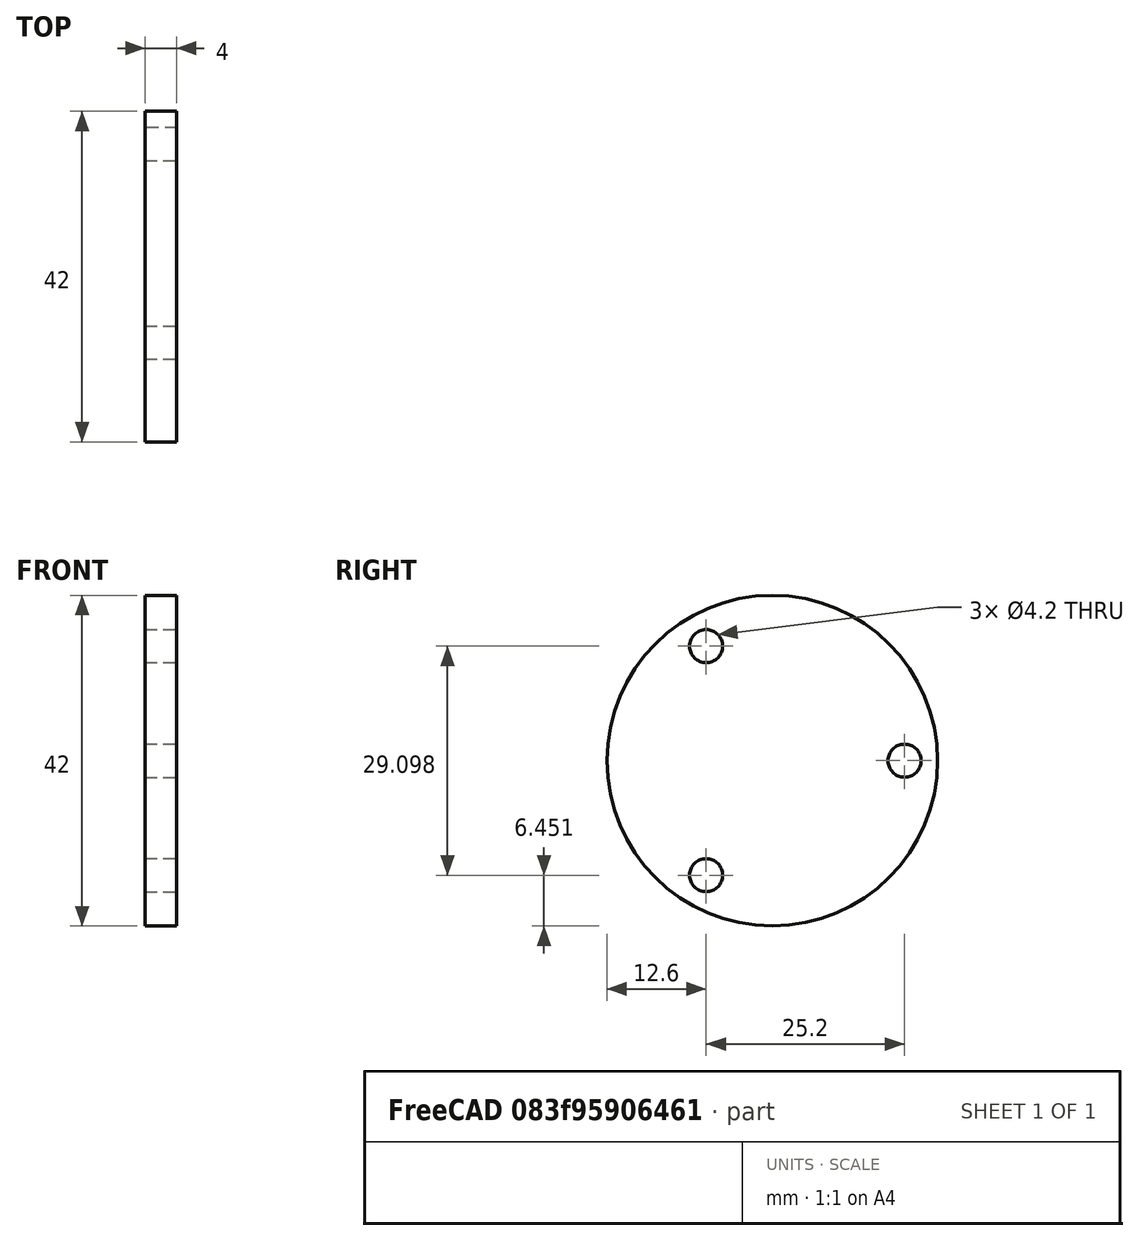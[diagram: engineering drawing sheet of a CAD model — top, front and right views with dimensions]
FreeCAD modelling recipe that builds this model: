
FCSTD DOCUMENT  (FreeCAD 0.19R21329 (Git))
Label: progetto
License: All rights reserved
LicenseURL: http://en.wikipedia.org/wiki/All_rights_reserved
objects: PartDesign::Body×2, Sketcher::SketchObject×2, Mesh::Feature×2, Part::Feature×1, PartDesign::Pad×1, PartDesign::Pocket×1, PartDesign::PolarPattern×1
note: 10 computed .brp shape members not serialized (recipe doc carries the construction recipe); baked Part::Feature solids carry a one-line shape summary decoded from their .brp

FEATURE [Part::Feature] Solid
  Placement = pos=(-4,0,0) rot=(0.57735,0.57735,0.57735;0rad)
  shape: bbox 21 x 16.5 x 15 mm, 4090 faces (baked)
FEATURE [PartDesign::Body] Body
  Group = -> [Solid]
  Origin = -> Origin
  Placement = pos=(0,-5,-7) rot=(0,0,1;0rad)
FEATURE [Sketcher::SketchObject] Sketch
  MapMode = 5
  Placement = pos=(0,0,0) rot=(0.57735,0.57735,0.57735;2.0944rad)
  Support = -> [YZ_Plane001]
  sketch-geometry (1):
    g0: Circle CenterX=0 CenterY=0 CenterZ=0 NormalX=0 NormalY=0 NormalZ=1 AngleXU=0 Radius=21
  constraints (1):
    c: Radius(g0) = 21
FEATURE [PartDesign::Pad] Pad
  Length = 4
  Length2 = 100
  Placement = pos=(0,0,0) rot=(0.57735,0.57735,0.57735;2.0944rad)
  Profile = -> Sketch
  Type = 0
FEATURE [Sketcher::SketchObject] Sketch001
  ExternalGeometry = -> [Pad]
  MapMode = 5
  Placement = pos=(4,-1.8e-15,1.3e-15) rot=(0.57735,0.57735,0.57735;2.0944rad)
  Support = -> [Pad]
  sketch-geometry (2):
    g0: Circle CenterX=16.8 CenterY=0 CenterZ=0 NormalX=0 NormalY=0 NormalZ=1 AngleXU=0 Radius=2.1
    g1: GeomPoint X=21 Y=0 Z=0
  constraints (5):
    c: Radius(g0) = 2.1
    c: PointOnObject(g0,g-1)
    c: PointOnObject(g1,g-1)
    c: PointOnObject(g1,g-3)
    c: DistanceX(g0,g1) = 4.2
FEATURE [PartDesign::Pocket] Pocket
  BaseFeature = -> Pad
  Length = 5
  Length2 = 100
  Placement = pos=(0,0,0) rot=(0.57735,0.57735,0.57735;2.0944rad)
  Profile = -> Sketch001
  Type = 1
FEATURE [PartDesign::PolarPattern] PolarPattern
  Angle = 360
  Axis = -> Sketch001 [N_Axis]
  BaseFeature = -> Pocket
  Occurrences = 3
  Originals = -> [Pocket]
  Placement = pos=(0,0,0) rot=(0.57735,0.57735,0.57735;2.0944rad)
FEATURE [PartDesign::Body] Body001
  Group = -> [Sketch,Pad,Sketch001,Pocket,PolarPattern]
  Origin = -> Origin001
  Tip = -> PolarPattern
FEATURE [Mesh::Feature] Mesh  label="Solid (Meshed)"
FEATURE [Mesh::Feature] Mesh001  label="PolarPattern (Meshed)"
